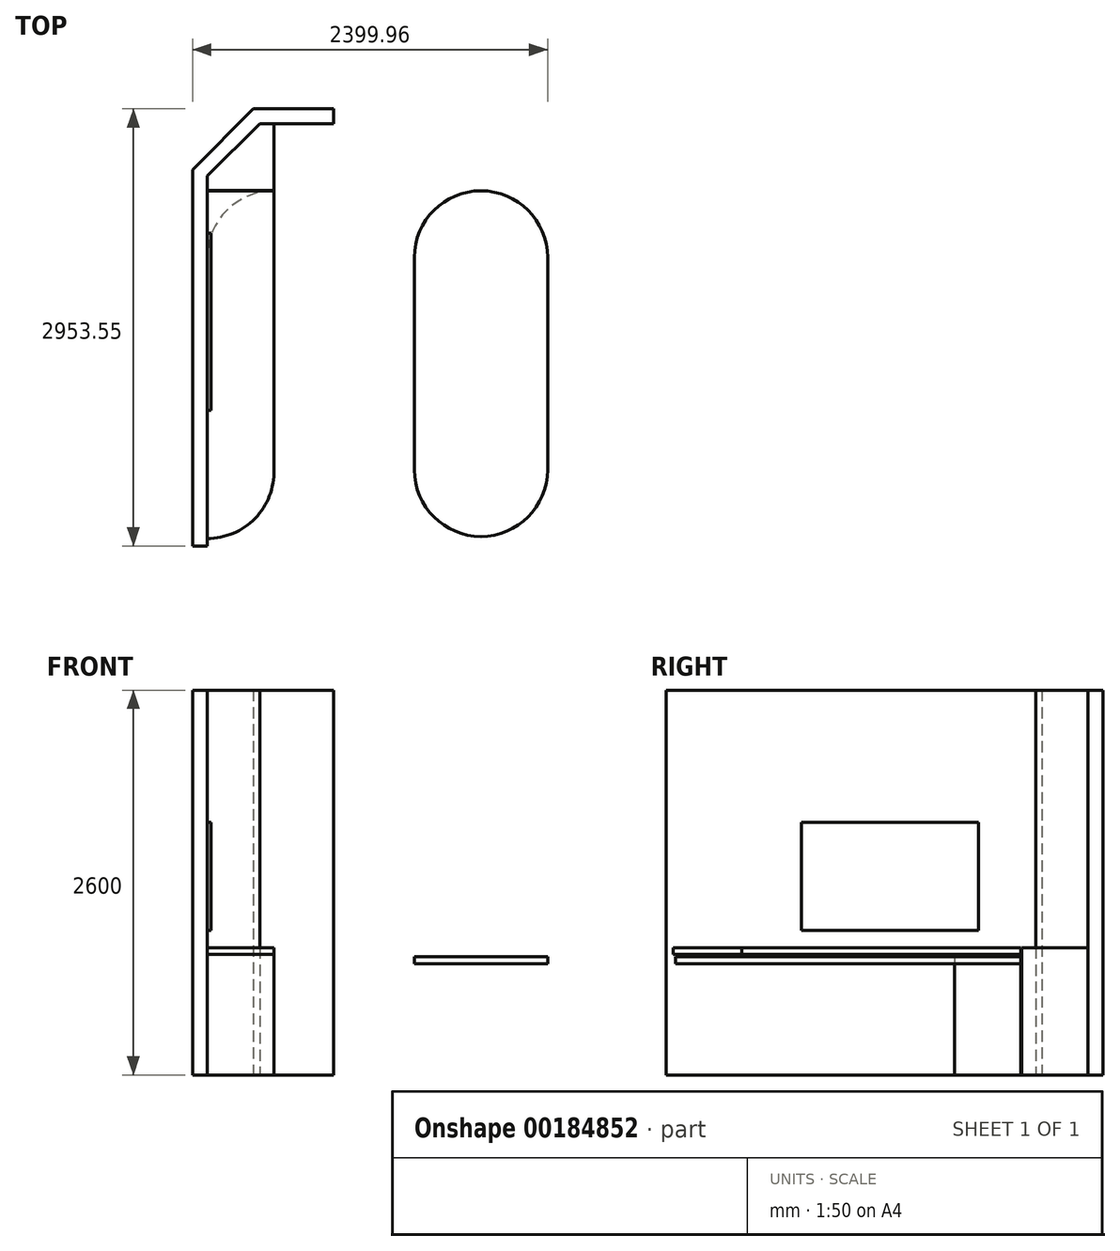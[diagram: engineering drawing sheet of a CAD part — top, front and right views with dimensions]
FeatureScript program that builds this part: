
annotation { "Feature Type Name" : "Feature", "Feature Type Description" : "" }
export const myFeature = defineFeature(function(context is Context, id is Id, definition is map)
    precondition{}
    {
        {
            var Q0;
            Q0=qCreatedBy(makeId("Top.planeOp"),FACE);
            var sketch = newSketch(context, id + "F0", { "sketchPlane" : qUnion([Q0])});
            skLineSegment(sketch, "E0", {"start": v(0, 0) * mm, "end": v(-500, 0) * mm});
            skLineSegment(sketch, "E1", {"start": v(-500, 0) * mm, "end": v(-853.55, -353.55) * mm});
            skLineSegment(sketch, "E2", {"start": v(-853.55, -353.55) * mm, "end": v(-853.55, -450) * mm});
            skLineSegment(sketch, "E3.top", {"start": v(0, 100) * mm, "end": v(-541.42, 100) * mm});
            skLineSegment(sketch, "E3.left", {"start": v(0, 0) * mm, "end": v(0, 100) * mm});
            skLineSegment(sketch, "E4.bottom", {"start": v(-853.55, -2853.55) * mm, "end": v(-953.55, -2853.55) * mm});
            skLineSegment(sketch, "E4.left", {"start": v(-853.55, -2853.55) * mm, "end": v(-853.55, -453.55) * mm});
            skLineSegment(sketch, "E4.right", {"start": v(-953.55, -2853.55) * mm, "end": v(-953.55, -312.13) * mm});
            skLineSegment(sketch, "E5", {"start": v(-953.55, -312.13) * mm, "end": v(-541.42, 100) * mm});
            skLineSegment(sketch, "E6", {"start": v(-403.55, -453.55) * mm, "end": v(-403.55, -2353.55) * mm});
            skLineSegment(sketch, "E7", {"start": v(-853.55, -450) * mm, "end": v(-403.55, -450) * mm});
            skLineSegment(sketch, "E8", {"start": v(-403.55, -450) * mm, "end": v(-403.55, 0) * mm});
            skLineSegment(sketch, "E9", {"start": v(-853.55, -453.55) * mm, "end": v(-403.55, -453.55) * mm});
            skLineSegment(sketch, "E10.trimOffspring", {"start": v(-853.55, -450) * mm, "end": v(-853.55, -353.55) * mm});
            skLineSegment(sketch, "E11.trimOffspring", {"start": v(-853.55, -453.55) * mm, "end": v(-853.55, -2853.55) * mm});
            skLineSegment(sketch, "E12", {"start": v(-551.1, -903.55) * mm, "end": v(-157.12, -903.55) * mm, "construction": true});
            skLineSegment(sketch, "E13", {"start": v(-403.55, -813.93) * mm, "end": v(-403.55, -970.7) * mm, "construction": true});
            skArc(sketch, "E14", {"start": v(-403.55, -453.55) * mm, "mid": v(-721.75, -585.36) * mm, "end": v(-853.55, -903.55) * mm});
            skLineSegment(sketch, "E15", {"start": v(-1047.55, -2803.55) * mm, "end": v(67.83, -2803.55) * mm, "construction": true});
            skLineSegment(sketch, "E16", {"start": v(-403.55, -2353.55) * mm, "end": v(-1099.6, -2353.55) * mm, "construction": true});
            skLineSegment(sketch, "E17", {"start": v(-853.55, -2551.44) * mm, "end": v(-853.55, -2155.26) * mm, "construction": true});
            skArc(sketch, "E18", {"start": v(-853.55, -2803.55) * mm, "mid": v(-530.44, -2666.85) * mm, "end": v(-403.55, -2339.75) * mm});
            skLineSegment(sketch, "E19", {"start": v(-853.55, -1614.75) * mm, "end": v(-403.55, -1614.75) * mm});
            skLineSegment(sketch, "E20", {"start": v(996.41, 0) * mm, "end": v(996.41, -3826.61) * mm, "construction": true});
            skLineSegment(sketch, "E21", {"start": v(232.92, -903.55) * mm, "end": v(2207.93, -903.55) * mm, "construction": true});
            skLineSegment(sketch, "E22", {"start": v(149.32, -2339.75) * mm, "end": v(2281.08, -2339.75) * mm, "construction": true});
            skLineSegment(sketch, "E23.bottom", {"start": v(996.41, -903.55) * mm, "end": v(546.41, -903.55) * mm});
            skLineSegment(sketch, "E23.top", {"start": v(996.41, -2339.75) * mm, "end": v(546.41, -2339.75) * mm});
            skLineSegment(sketch, "E23.left", {"start": v(996.41, -903.55) * mm, "end": v(996.41, -2339.75) * mm});
            skLineSegment(sketch, "E23.right", {"start": v(546.41, -903.55) * mm, "end": v(546.41, -2339.75) * mm});
            skArc(sketch, "E24", {"start": v(546.41, -903.55) * mm, "mid": v(678.21, -585.36) * mm, "end": v(996.41, -453.55) * mm});
            skArc(sketch, "E25", {"start": v(546.41, -2339.75) * mm, "mid": v(678.21, -2657.94) * mm, "end": v(996.41, -2789.75) * mm});
            skLineSegment(sketch, "E26", {"start": v(996.41, -2789.75) * mm, "end": v(996.41, -453.55) * mm});
            skArc(sketch, "E27.MirrorCS", {"start": v(1446.41, -903.55) * mm, "mid": v(1314.61, -585.36) * mm, "end": v(996.41, -453.55) * mm});
            skLineSegment(sketch, "E28.MirrorCS", {"start": v(1446.41, -903.55) * mm, "end": v(1446.41, -2339.75) * mm});
            skArc(sketch, "E29.MirrorCS", {"start": v(1446.41, -2339.75) * mm, "mid": v(1314.61, -2657.94) * mm, "end": v(996.41, -2789.75) * mm});
            skLineSegment(sketch, "E30", {"start": v(-541.42, 100) * mm, "end": v(-953.55, -312.13) * mm});
            skLineSegment(sketch, "E31", {"start": v(-953.55, -2853.55) * mm, "end": v(-853.55, -2853.55) * mm});
            skLineSegment(sketch, "E32", {"start": v(-853.55, -353.55) * mm, "end": v(-500, 0) * mm});
            skLineSegment(sketch, "E33.left", {"start": v(-853.55, -2853.55) * mm, "end": v(-853.55, -353.55) * mm});
            skSolve(sketch);
        }
        {
            var Q0;
            Q0=makeQuery(id+"F0.imprint","IMPRINT",FACE,{"disambiguationData":[TD([[makeQuery(id+"F0.imprint","IMPRINT",EDGE,{"derivedFrom":sQuery(id+"F0.wireOp",EDGE,"E3.top")}),1.0]])]});
            extrude(context, id + "F1", {"entities" : qUnion([Q0]), "depth" : 2600 * mm});
        }
        {
            var Q0;
            {var subQ2=sQuery(id+"F0.wireOp",EDGE,"E7");Q0=makeQuery(id+"F0.imprint","IMPRINT",FACE,{"disambiguationData":[TD([[makeQuery(id+"F0.imprint","IMPRINT",EDGE,{"derivedFrom":subQ2}),1.0]])]});}
            var Q1;
            {var subQ0=sQuery(id+"F0.wireOp",EDGE,"E9");Q1=makeQuery(id+"F0.imprint","IMPRINT",FACE,{"disambiguationData":[TD([[makeQuery(id+"F0.imprint","IMPRINT",EDGE,{"derivedFrom":subQ0}),-1.0]])]});}
            var Q2;
            {var subQ0=sQuery(id+"F0.wireOp",EDGE,"E14");Q2=makeQuery(id+"F0.imprint","IMPRINT",FACE,{"disambiguationData":[TD([[makeQuery(id+"F0.imprint","IMPRINT",EDGE,{"derivedFrom":subQ0}),1.0]])]});}
            var Q3;
            {var subQ0=sQuery(id+"F0.wireOp",EDGE,"E18");Q3=makeQuery(id+"F0.imprint","IMPRINT",FACE,{"disambiguationData":[TD([[makeQuery(id+"F0.imprint","IMPRINT",EDGE,{"derivedFrom":subQ0}),1.0]])]});}
            extrude(context, id + "F2", {"entities" : qUnion([Q0, Q1, Q2, Q3]), "depth" : 860 * mm});
        }
        {
            var Q0;
            {var subQ0=sQuery(id+"F0.wireOp",EDGE,"E27.MirrorCS");Q0=makeQuery(id+"F0.imprint","IMPRINT",FACE,{"disambiguationData":[TD([[makeQuery(id+"F0.imprint","IMPRINT",EDGE,{"derivedFrom":subQ0}),1.0]])]});}
            var Q1;
            {var subQ0=sQuery(id+"F0.wireOp",EDGE,"E23.bottom");Q1=makeQuery(id+"F0.imprint","IMPRINT",FACE,{"disambiguationData":[TD([[makeQuery(id+"F0.imprint","IMPRINT",EDGE,{"derivedFrom":subQ0}),1.0]])]});}
            var Q2;
            {var subQ0=sQuery(id+"F0.wireOp",EDGE,"E23.bottom");Q2=makeQuery(id+"F0.imprint","IMPRINT",FACE,{"disambiguationData":[TD([[makeQuery(id+"F0.imprint","IMPRINT",EDGE,{"derivedFrom":subQ0}),-1.0]])]});}
            var Q3;
            {var subQ0=sQuery(id+"F0.wireOp",EDGE,"E23.top");Q3=makeQuery(id+"F0.imprint","IMPRINT",FACE,{"disambiguationData":[TD([[makeQuery(id+"F0.imprint","IMPRINT",EDGE,{"derivedFrom":subQ0}),1.0]])]});}
            extrude(context, id + "F3", {"entities" : qUnion([Q0, Q1, Q2, Q3]), "depth" : 800 * mm});
        }
        {
            var Q0;
            {var subQ0=sQuery(id+"F0.wireOp",EDGE,"E18");Q0=makeQuery(id+"F0.imprint","IMPRINT",FACE,{"disambiguationData":[TD([[makeQuery(id+"F0.imprint","IMPRINT",EDGE,{"derivedFrom":subQ0}),1.0]])]});}
            var Q1;
            {var subQ0=sQuery(id+"F0.wireOp",EDGE,"E14");Q1=makeQuery(id+"F0.imprint","IMPRINT",FACE,{"disambiguationData":[TD([[makeQuery(id+"F0.imprint","IMPRINT",EDGE,{"derivedFrom":subQ0}),1.0]])]});}
            extrude(context, id + "F4", {"entities" : qUnion([Q0, Q1]), "operationType" : NewBodyOperationType.REMOVE, "depth" : 815 * mm});
        }
        {
            var Q0;
            {var subQ0=sQuery(id+"F0.wireOp",EDGE,"E23.bottom");Q0=makeQuery(id+"F0.imprint","IMPRINT",FACE,{"disambiguationData":[TD([[makeQuery(id+"F0.imprint","IMPRINT",EDGE,{"derivedFrom":subQ0}),1.0]])]});}
            var Q1;
            {var subQ0=sQuery(id+"F0.wireOp",EDGE,"E27.MirrorCS");Q1=makeQuery(id+"F0.imprint","IMPRINT",FACE,{"disambiguationData":[TD([[makeQuery(id+"F0.imprint","IMPRINT",EDGE,{"derivedFrom":subQ0}),1.0]])]});}
            var Q2;
            {var subQ0=sQuery(id+"F0.wireOp",EDGE,"E23.top");Q2=makeQuery(id+"F0.imprint","IMPRINT",FACE,{"disambiguationData":[TD([[makeQuery(id+"F0.imprint","IMPRINT",EDGE,{"derivedFrom":subQ0}),1.0]])]});}
            var Q3;
            {var subQ0=sQuery(id+"F0.wireOp",EDGE,"E23.bottom");Q3=makeQuery(id+"F0.imprint","IMPRINT",FACE,{"disambiguationData":[TD([[makeQuery(id+"F0.imprint","IMPRINT",EDGE,{"derivedFrom":subQ0}),-1.0]])]});}
            extrude(context, id + "F5", {"entities" : qUnion([Q0, Q1, Q2, Q3]), "operationType" : NewBodyOperationType.REMOVE, "depth" : 750 * mm});
        }
        {
            var Q0;
            Q0=makeQuery(id+"F1.opExtrude","SWEPT_FACE",FACE,{"disambiguationData":[OSD([sQuery(id+"F0.wireOp",EDGE,"E33.left")])]});
            var sketch = newSketch(context, id + "F6", { "sketchPlane" : qUnion([Q0])});
            skLineSegment(sketch, "E34.bottom", {"start": v(-1938.07, 976.26) * mm, "end": v(-740.2, 976.26) * mm});
            skLineSegment(sketch, "E34.top", {"start": v(-1938.07, 1705.61) * mm, "end": v(-740.2, 1705.61) * mm});
            skLineSegment(sketch, "E34.left", {"start": v(-1938.07, 976.26) * mm, "end": v(-1938.07, 1705.61) * mm});
            skLineSegment(sketch, "E34.right", {"start": v(-740.2, 976.26) * mm, "end": v(-740.2, 1705.61) * mm});
            skSolve(sketch);
        }
        {
            var Q0;
            Q0 = qSketchRegion(id + "F6", true);
            extrude(context, id + "F7", {"entities" : qUnion([Q0]), "depth" : 25 * mm});
        }
    });
